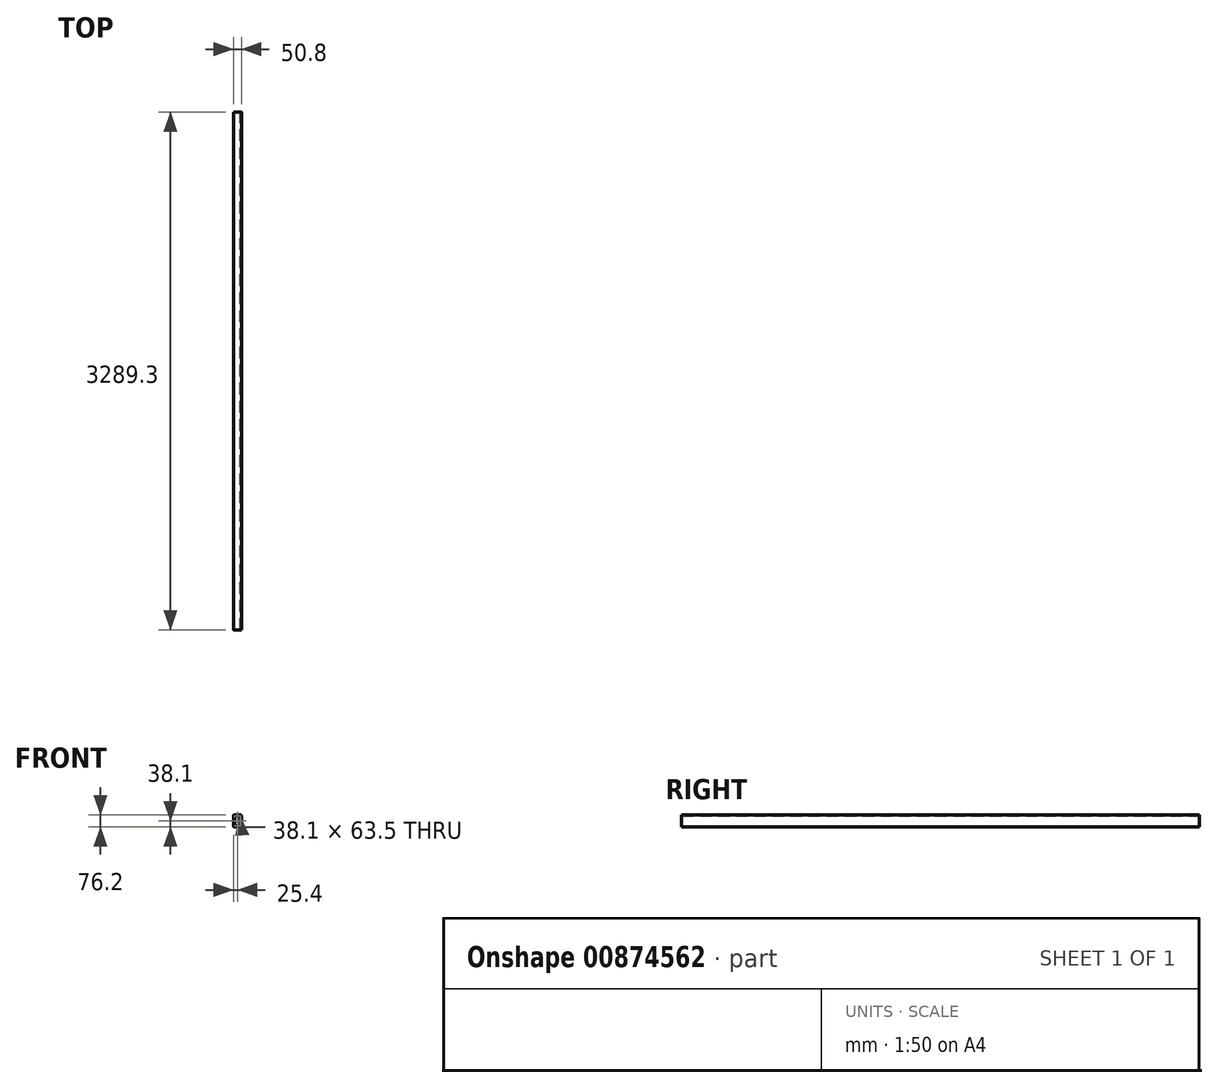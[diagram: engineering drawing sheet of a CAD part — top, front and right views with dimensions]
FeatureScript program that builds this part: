
annotation { "Feature Type Name" : "Feature", "Feature Type Description" : "" }
export const myFeature = defineFeature(function(context is Context, id is Id, definition is map)
    precondition{}
    {
        {
            var Q0;
            Q0=qCreatedBy(makeId("Front.planeOp"),FACE);
            var sketch = newSketch(context, id + "F0", { "sketchPlane" : qUnion([Q0])});
            skLineSegment(sketch, "E0.bottom", {"start": v(-19.05, 38.1) * mm, "end": v(19.05, 38.1) * mm});
            skLineSegment(sketch, "E0.top", {"start": v(-19.05, -38.1) * mm, "end": v(19.05, -38.1) * mm});
            skLineSegment(sketch, "E0.left", {"start": v(-25.4, 31.75) * mm, "end": v(-25.4, -31.75) * mm});
            skLineSegment(sketch, "E0.right", {"start": v(25.4, 31.75) * mm, "end": v(25.4, -31.75) * mm});
            skPoint(sketch, "E0.middle", {"position": v(0, 0) * mm});
            skLineSegment(sketch, "E1.bottom", {"start": v(-19.05, 31.75) * mm, "end": v(19.05, 31.75) * mm});
            skLineSegment(sketch, "E1.top", {"start": v(-19.05, -31.75) * mm, "end": v(19.05, -31.75) * mm});
            skLineSegment(sketch, "E1.left", {"start": v(-19.05, 31.75) * mm, "end": v(-19.05, -31.75) * mm});
            skLineSegment(sketch, "E1.right", {"start": v(19.05, 31.75) * mm, "end": v(19.05, -31.75) * mm});
            skPoint(sketch, "E2.visualSharp", {"position": v(-25.4, 38.1) * mm});
            skArc(sketch, "E2.filletArc", {"start": v(-19.05, 38.1) * mm, "mid": v(-23.54, 36.24) * mm, "end": v(-25.4, 31.75) * mm});
            skPoint(sketch, "E3.visualSharp", {"position": v(25.4, 38.1) * mm});
            skArc(sketch, "E3.filletArc", {"start": v(25.4, 31.75) * mm, "mid": v(23.54, 36.24) * mm, "end": v(19.05, 38.1) * mm});
            skPoint(sketch, "E4.visualSharp", {"position": v(25.4, -38.1) * mm});
            skArc(sketch, "E4.filletArc", {"start": v(19.05, -38.1) * mm, "mid": v(23.54, -36.24) * mm, "end": v(25.4, -31.75) * mm});
            skPoint(sketch, "E5.visualSharp", {"position": v(-25.4, -38.1) * mm});
            skArc(sketch, "E5.filletArc", {"start": v(-25.4, -31.75) * mm, "mid": v(-23.54, -36.24) * mm, "end": v(-19.05, -38.1) * mm});
            skSolve(sketch);
        }
        {
            var Q0;
            Q0=makeQuery(id+"F0.imprint","IMPRINT",FACE,{"disambiguationData":[TD([[makeQuery(id+"F0.imprint","IMPRINT",EDGE,{"derivedFrom":sQuery(id+"F0.wireOp",EDGE,"E0.bottom")}),-1.0]])]});
            extrude(context, id + "F1", {"entities" : qUnion([Q0]), "depth" : 3289.3 * mm, "offsetDistance" : 25.4 * mm});
        }
    });
